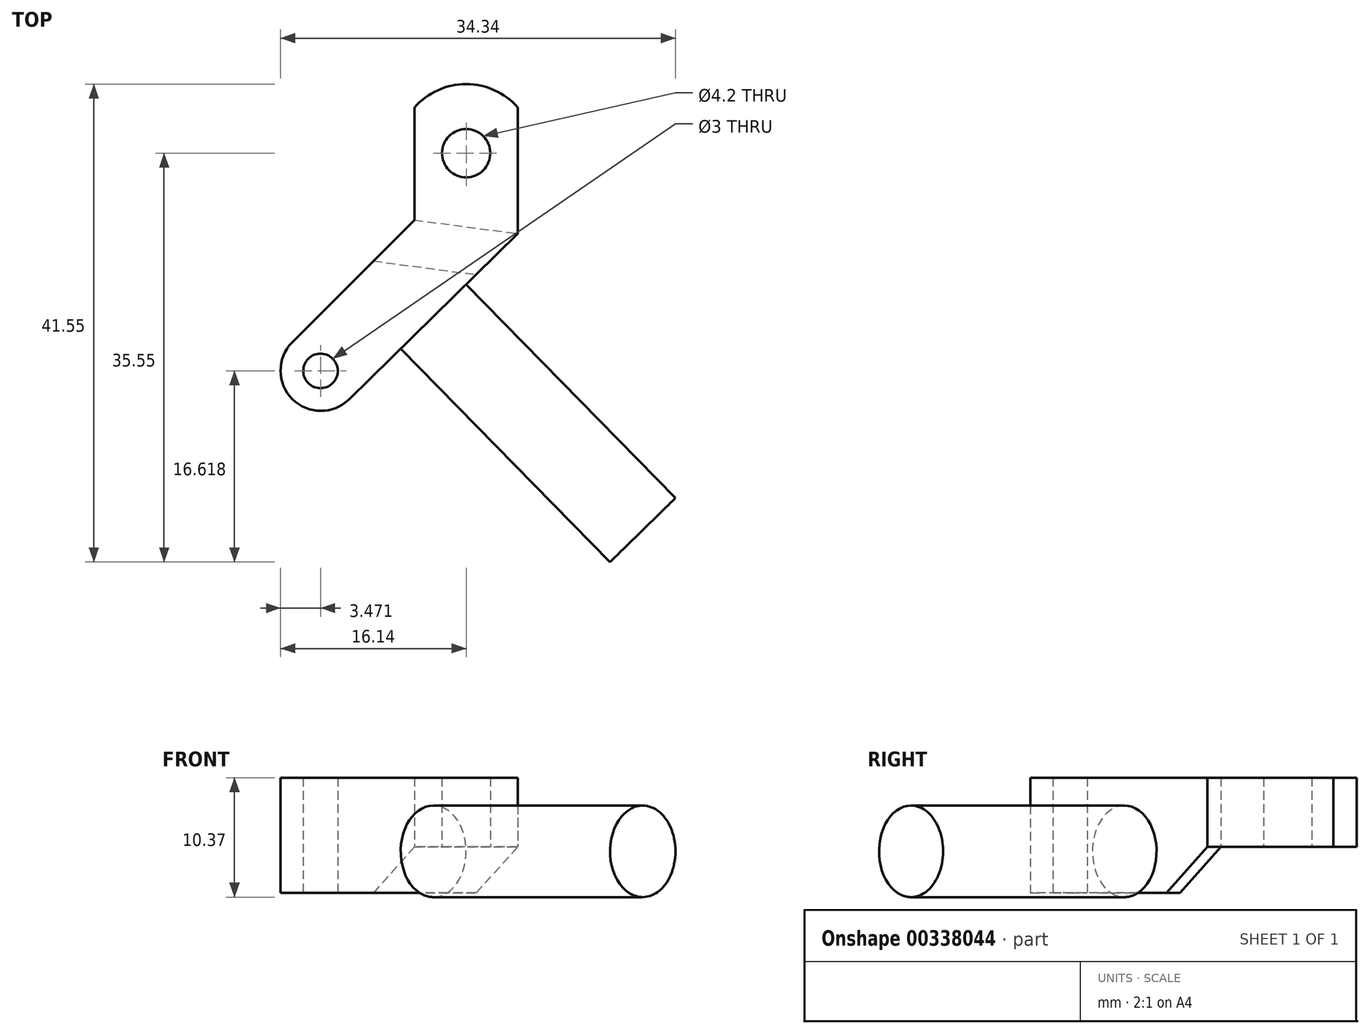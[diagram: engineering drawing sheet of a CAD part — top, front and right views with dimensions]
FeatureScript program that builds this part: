
annotation { "Feature Type Name" : "Feature", "Feature Type Description" : "" }
export const myFeature = defineFeature(function(context is Context, id is Id, definition is map)
    precondition{}
    {
        {
            var Q0;
            Q0=qCreatedBy(makeId("Top.planeOp"),FACE);
            var sketch = newSketch(context, id + "F0", { "sketchPlane" : qUnion([Q0])});
            skPoint(sketch, "E0.middle", {"position": v(0, 0) * mm});
            skCircle(sketch, "E1", {"center": v(0, 0) * mm, "radius": 2.1 * mm});
            skArc(sketch, "E2", {"start": v(4.5, 3.97) * mm, "mid": v(0, 6) * mm, "end": v(-4.5, 3.97) * mm});
            skLineSegment(sketch, "E3", {"start": v(4.5, 0) * mm, "end": v(4.5, 3.97) * mm});
            skLineSegment(sketch, "E4", {"start": v(0, 14.22) * mm, "end": v(0, -15.58) * mm, "construction": true});
            skLineSegment(sketch, "E5.MirrorCS", {"start": v(-4.5, 0) * mm, "end": v(-4.5, 3.97) * mm});
            skLineSegment(sketch, "E6", {"start": v(-4.5, 0) * mm, "end": v(-4.5, -5.81) * mm});
            skLineSegment(sketch, "E7", {"start": v(4.5, 0) * mm, "end": v(4.5, -7) * mm});
            skLineSegment(sketch, "E8", {"start": v(4.5, -7) * mm, "end": v(-10.2, -21.4) * mm});
            skCircle(sketch, "E9", {"center": v(-12.67, -18.93) * mm, "radius": 1.5 * mm});
            skLineSegment(sketch, "E10", {"start": v(-15.14, -16.46) * mm, "end": v(-4.5, -5.81) * mm});
            skArc(sketch, "E11", {"start": v(-15.14, -16.46) * mm, "mid": v(-15.12, -21.38) * mm, "end": v(-10.2, -21.4) * mm});
            skSolve(sketch);
        }
        {
            var Q0;
            Q0=makeQuery(id+"F0.imprint","IMPRINT",FACE,{"disambiguationData":[TD([[makeQuery(id+"F0.imprint","IMPRINT",EDGE,{"derivedFrom":sQuery(id+"F0.wireOp",EDGE,"E1")}),-1.0]])]});
            extrude(context, id + "F1", {"entities" : qUnion([Q0]), "depth" : 6 * mm});
        }
        {
            var Q0;
            Q0=makeQuery(id+"F1.opExtrude","SWEPT_FACE",FACE,{"disambiguationData":[OSD([sQuery(id+"F0.wireOp",EDGE,"E8")])]});
            var sketch = newSketch(context, id + "F2", { "sketchPlane" : qUnion([Q0])});
            skCircle(sketch, "E12", {"center": v(-11.98, -0.39) * mm, "radius": 3.98 * mm});
            skPoint(sketch, "E12.centerSnap0", {"position": v(-11.98, 0) * mm});
            skSolve(sketch);
        }
        {
            var Q0;
            Q0=qSketchRegion(id+"F2",true);
            extrude(context, id + "F3", {"entities" : qUnion([Q0]), "operationType" : NewBodyOperationType.ADD, "depth" : 26 * mm});
        }
        {
            var Q0;
            Q0=makeQuery(id+"F1.opExtrude","CAP_FACE",FACE,{"disambiguationData":[OSD([sQuery(id+"F0.wireOp",EDGE,"E1"),sQuery(id+"F0.wireOp",EDGE,"E2"),sQuery(id+"F0.wireOp",EDGE,"E3"),sQuery(id+"F0.wireOp",EDGE,"E5.MirrorCS"),sQuery(id+"F0.wireOp",EDGE,"E6"),sQuery(id+"F0.wireOp",EDGE,"E7"),sQuery(id+"F0.wireOp",EDGE,"E8"),sQuery(id+"F0.wireOp",EDGE,"E9"),sQuery(id+"F0.wireOp",EDGE,"E10"),sQuery(id+"F0.wireOp",EDGE,"E11")])],"isStart":true});
            var sketch = newSketch(context, id + "F4", { "sketchPlane" : qUnion([Q0])});
            skArc(sketch, "E13.0", {"start": v(-15.14, 16.46) * mm, "mid": v(-15.12, 21.38) * mm, "end": v(-10.2, 21.4) * mm});
            skLineSegment(sketch, "E14.0", {"start": v(4.5, 7) * mm, "end": v(-10.2, 21.4) * mm});
            skLineSegment(sketch, "E15.0", {"start": v(-15.14, 16.46) * mm, "end": v(-4.5, 5.81) * mm});
            skLineSegment(sketch, "E16", {"start": v(-4.5, 5.81) * mm, "end": v(4.5, 7) * mm});
            skCircle(sketch, "E17.0", {"center": v(-12.67, 18.93) * mm, "radius": 1.5 * mm});
            skSolve(sketch);
        }
        {
            var Q0;
            Q0=qSketchRegion(id+"F4",true);
            extrude(context, id + "F5", {"entities" : qUnion([Q0]), "operationType" : NewBodyOperationType.ADD, "depth" : 4 * mm});
        }
        {
            var Q0;
            Q0=makeQuery(id+"F5.opExtrude","CAP_EDGE",EDGE,{"disambiguationData":[OSD([sQuery(id+"F4.wireOp",EDGE,"E16")])],"isStart":false});
            chamfer(context, id + "F6", {"entities" : qUnion([Q0]), "width" : 4 * mm, "tangentPropagation" : true});
        }
    });
